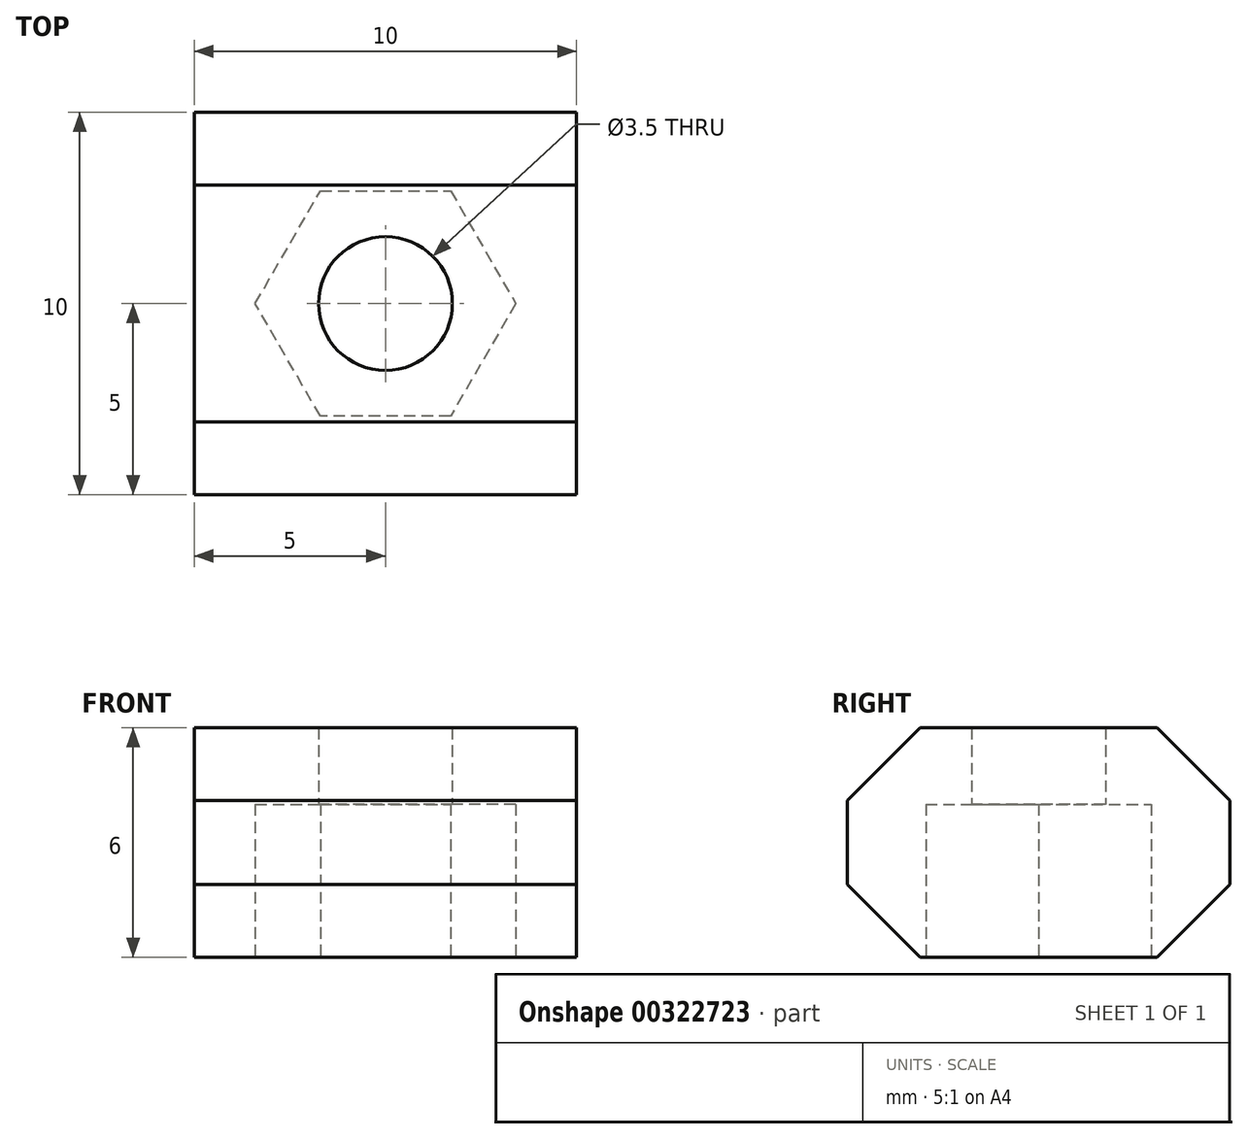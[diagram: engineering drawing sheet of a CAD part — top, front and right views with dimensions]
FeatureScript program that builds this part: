
annotation { "Feature Type Name" : "Feature", "Feature Type Description" : "" }
export const myFeature = defineFeature(function(context is Context, id is Id, definition is map)
    precondition{}
    {
        {
            var Q0;
            Q0=qCreatedBy(makeId("Top.planeOp"),FACE);
            var sketch = newSketch(context, id + "F0", { "sketchPlane" : qUnion([Q0])});
            skCircle(sketch, "E0.cCircle", {"center": v(0, 0) * mm, "radius": 2.95 * mm, "construction": true});
            skLineSegment(sketch, "E0.0", {"start": v(-1.7, 2.95) * mm, "end": v(1.7, 2.95) * mm});
            skLineSegment(sketch, "E0.1", {"start": v(1.7, 2.95) * mm, "end": v(3.4, 0) * mm});
            skLineSegment(sketch, "E0.2", {"start": v(3.4, 0) * mm, "end": v(1.7, -2.95) * mm});
            skLineSegment(sketch, "E0.3", {"start": v(1.7, -2.95) * mm, "end": v(-1.7, -2.95) * mm});
            skLineSegment(sketch, "E0.4", {"start": v(-1.7, -2.95) * mm, "end": v(-3.4, 0) * mm});
            skLineSegment(sketch, "E0.5", {"start": v(-3.4, 0) * mm, "end": v(-1.7, 2.95) * mm});
            skPoint(sketch, "E0.0.midPoint", {"position": v(0, 2.95) * mm});
            skLineSegment(sketch, "E1.bottom", {"start": v(5, 5) * mm, "end": v(-5, 5) * mm});
            skLineSegment(sketch, "E1.top", {"start": v(5, -5) * mm, "end": v(-5, -5) * mm});
            skLineSegment(sketch, "E1.left", {"start": v(5, 5) * mm, "end": v(5, -5) * mm});
            skLineSegment(sketch, "E1.right", {"start": v(-5, 5) * mm, "end": v(-5, -5) * mm});
            skCircle(sketch, "E2", {"center": v(0, 0) * mm, "radius": 1.75 * mm});
            skSolve(sketch);
        }
        {
            var Q0;
            Q0=makeQuery(id+"F0.imprint","IMPRINT",FACE,{"disambiguationData":[TD([[makeQuery(id+"F0.imprint","IMPRINT",EDGE,{"derivedFrom":sQuery(id+"F0.wireOp",EDGE,"E0.0")}),1.0]])]});
            var Q1;
            Q1=makeQuery(id+"F0.imprint","IMPRINT",FACE,{"disambiguationData":[TD([[makeQuery(id+"F0.imprint","IMPRINT",EDGE,{"derivedFrom":sQuery(id+"F0.wireOp",EDGE,"E0.0")}),-1.0]])]});
            extrude(context, id + "F1", {"entities" : qUnion([Q0, Q1]), "depth" : 6 * mm});
        }
        {
            var Q0;
            Q0=makeQuery(id+"F0.imprint","IMPRINT",FACE,{"disambiguationData":[TD([[makeQuery(id+"F0.imprint","IMPRINT",EDGE,{"derivedFrom":sQuery(id+"F0.wireOp",EDGE,"E0.0")}),-1.0]])]});
            extrude(context, id + "F2", {"entities" : qUnion([Q0]), "operationType" : NewBodyOperationType.REMOVE, "depth" : 4 * mm});
        }
        {
            var Q0;
            Q0=makeQuery(id+"F1.opExtrude","CAP_EDGE",EDGE,{"disambiguationData":[OSD([sQuery(id+"F0.wireOp",EDGE,"E1.bottom")])],"isStart":true});
            var Q1;
            Q1=makeQuery(id+"F1.opExtrude","CAP_EDGE",EDGE,{"disambiguationData":[OSD([sQuery(id+"F0.wireOp",EDGE,"E1.top")])],"isStart":true});
            var Q2;
            Q2=makeQuery(id+"F1.opExtrude","CAP_EDGE",EDGE,{"disambiguationData":[OSD([sQuery(id+"F0.wireOp",EDGE,"E1.bottom")])],"isStart":false});
            var Q3;
            Q3=makeQuery(id+"F1.opExtrude","CAP_EDGE",EDGE,{"disambiguationData":[OSD([sQuery(id+"F0.wireOp",EDGE,"E1.top")])],"isStart":false});
            chamfer(context, id + "F3", {"entities" : qUnion([Q0, Q1, Q2, Q3]), "width" : 1.9 * mm, "tangentPropagation" : true});
        }
    });
